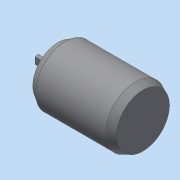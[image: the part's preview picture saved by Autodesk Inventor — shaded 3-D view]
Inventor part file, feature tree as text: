
AUTODESK INVENTOR PART (.ipt)
format: ipt  version: 2017 (Build 210142000, 142)  size: 165,888 bytes
history: native  units: in
note: dims shown in document units (in); Inventor stores cm internally (conversion verified against a paired STEP export)
features: sketch x4, extrude x3, other x1, plane x1
ambient origin geometry x8: Origin, YZ Plane, XZ Plane, XY Plane, X Axis, Y Axis, Z Axis, Center Point
bodies: Body1 (feature_tree)
feature tree (9):
  other  "motor body"
  extrude  "axis slot"  Depth=0.315in
  extrude  "mounting holes"  Depth=0.1575in
  plane  "Work Plane1"
  extrude  "cable hole"  Depth=1.2402in
  sketch  "Sketch1"  dims[d7=0.8858in d9=0.315in]
  sketch  "Sketch4"  dims[d10=2.9134in d14=0.1575in]
  sketch  "Sketch5"  dims[d15=4.4094in d16=1.2402in]
  sketch  "Sketch6"  dims[d17=1.1024in d18=0.8661in d19=90.0deg d20=0.9843in d21=0.0in d22=0.125in d23=0.7874in d25=1.2205in d26=0.7874in d28=1.2205in d31=0.6102in d32=0.6102in d33=0.1575in d34=0.0in d35=0.7874in d36=0.2165in d37=0.0591in d38=0.3937in d39=0.0in]
